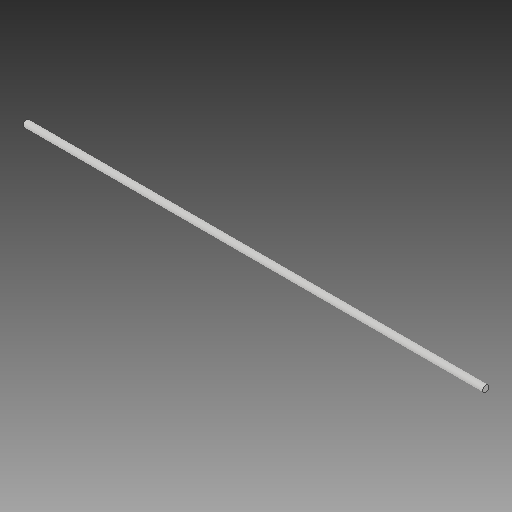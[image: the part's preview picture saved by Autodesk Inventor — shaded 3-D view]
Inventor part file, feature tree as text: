
AUTODESK INVENTOR PART (.ipt)
format: ipt  version: 2017 (Build 210142000, 142)  size: 89,088 bytes
history: native  units: in
note: dims shown in document units (in); Inventor stores cm internally (conversion verified against a paired STEP export)
features: extrude x1, sketch x1
ambient origin geometry x8: Origin, YZ Plane, XZ Plane, XY Plane, X Axis, Y Axis, Z Axis, Center Point
bodies: Solid1 (feature_tree)
feature tree (2):
  extrude  "Extrusion1"  Depth=18.0in TaperAngle=0.0deg
  sketch  "Sketch1"  dims[d0=0.25in d1=18.0in d2=0.0in]
